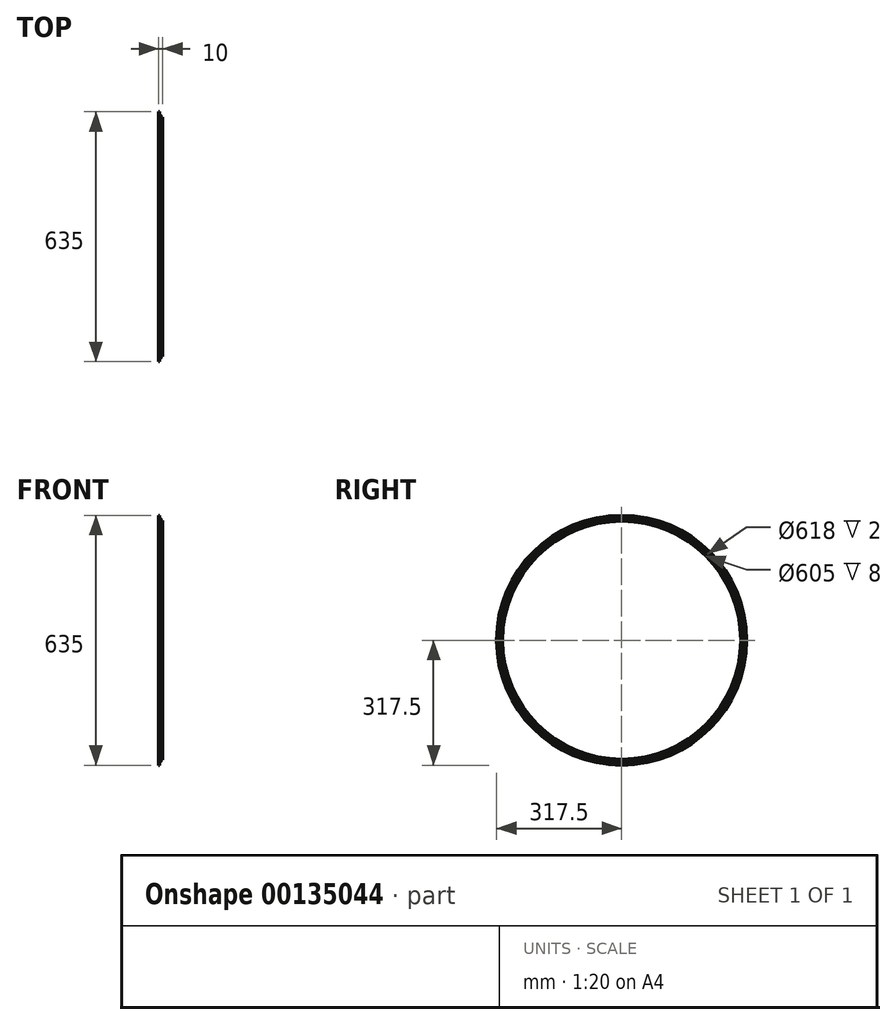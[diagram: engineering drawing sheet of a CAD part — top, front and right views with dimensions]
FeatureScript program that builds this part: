
annotation { "Feature Type Name" : "Feature", "Feature Type Description" : "" }
export const myFeature = defineFeature(function(context is Context, id is Id, definition is map)
    precondition{}
    {
        {
            var Q0;
            Q0=qCreatedBy(makeId("Front.planeOp"),FACE);
            var sketch = newSketch(context, id + "F0", { "sketchPlane" : qUnion([Q0])});
            skLineSegment(sketch, "E0", {"start": v(-8, 317.5) * mm, "end": v(-8, 311) * mm});
            skLineSegment(sketch, "E1", {"start": v(-8, 311) * mm, "end": v(-6, 311) * mm});
            skLineSegment(sketch, "E2", {"start": v(-6, 311) * mm, "end": v(-6, 304.5) * mm});
            skLineSegment(sketch, "E3", {"start": v(-6, 304.5) * mm, "end": v(0, 304.5) * mm});
            skLineSegment(sketch, "E4", {"start": v(0, 304.5) * mm, "end": v(0, 302.5) * mm});
            skLineSegment(sketch, "E5", {"start": v(0, 302.5) * mm, "end": v(-8, 302.5) * mm});
            skLineSegment(sketch, "E6", {"start": v(-8, 302.5) * mm, "end": v(-8, 309) * mm});
            skLineSegment(sketch, "E7", {"start": v(-8, 309) * mm, "end": v(-10, 309) * mm});
            skLineSegment(sketch, "E8", {"start": v(-10, 309) * mm, "end": v(-10, 317.5) * mm});
            skLineSegment(sketch, "E9", {"start": v(-10, 317.5) * mm, "end": v(-8, 317.5) * mm});
            skSolve(sketch);
        }
        {
            var Q0;
            Q0=qCreatedBy(makeId("Front.planeOp"),FACE);
            var sketch = newSketch(context, id + "F1", { "sketchPlane" : qUnion([Q0])});
            skLineSegment(sketch, "E10", {"start": v(-9.96, 0) * mm, "end": v(11.51, 0) * mm});
            skSolve(sketch);
        }
        {
            var Q0;
            Q0=makeQuery(id+"F0.imprint","IMPRINT",FACE,{"disambiguationData":[TD([[makeQuery(id+"F0.imprint","IMPRINT",EDGE,{"derivedFrom":sQuery(id+"F0.wireOp",EDGE,"E0")}),-1.0]])]});
            var Q1;
            Q1=sQuery(id+"F1.wireOp",EDGE,"E10");
            revolve(context, id + "F2", {"entities" : qUnion([Q0]), "axis" : qUnion([Q1]), "revolveType" : RevolveType.FULL});
        }
    });
